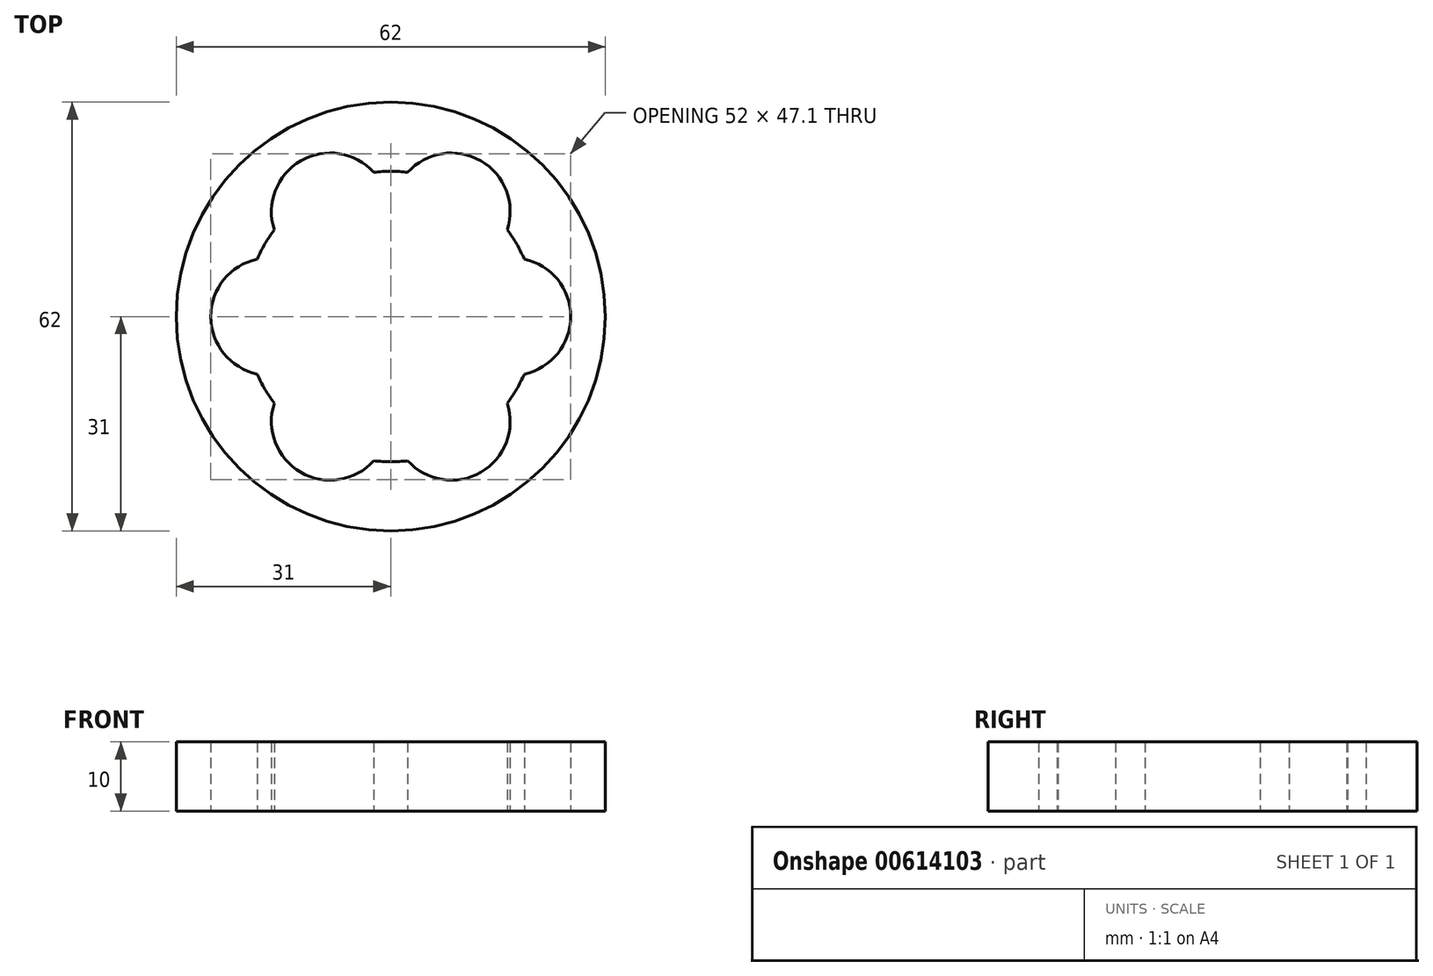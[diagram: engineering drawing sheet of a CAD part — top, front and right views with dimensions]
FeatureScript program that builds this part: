
annotation { "Feature Type Name" : "Feature", "Feature Type Description" : "" }
export const myFeature = defineFeature(function(context is Context, id is Id, definition is map)
    precondition{}
    {
        {
            var Q0;
            Q0=qCreatedBy(makeId("Top.planeOp"),FACE);
            var sketch = newSketch(context, id + "F0", { "sketchPlane" : qUnion([Q0])});
            skCircle(sketch, "E0", {"center": v(0, 0) * mm, "radius": 7 * mm});
            skCircle(sketch, "E1", {"center": v(17.5, 0) * mm, "radius": 8.5 * mm});
            skCircle(sketch, "E2.1.0", {"center": v(8.75, 15.16) * mm, "radius": 8.5 * mm});
            skCircle(sketch, "E2.2.0", {"center": v(-8.75, 15.16) * mm, "radius": 8.5 * mm});
            skCircle(sketch, "E2.3.0", {"center": v(-17.5, 0) * mm, "radius": 8.5 * mm});
            skCircle(sketch, "E2.4.0", {"center": v(-8.75, -15.16) * mm, "radius": 8.5 * mm});
            skCircle(sketch, "E2.5.0", {"center": v(8.75, -15.16) * mm, "radius": 8.5 * mm});
            skCircle(sketch, "E3", {"center": v(0, 0) * mm, "radius": 21 * mm});
            skCircle(sketch, "E4", {"center": v(0, 0) * mm, "radius": 31 * mm});
            skSolve(sketch);
        }
        {
            var Q0;
            Q0=makeQuery(id+"F0.imprint","IMPRINT",FACE,{"disambiguationData":[TD([[makeQuery(id+"F0.imprint","IMPRINT",EDGE,{"derivedFrom":sQuery(id+"F0.wireOp",EDGE,"VCIgbswB-IoET-C4wx-rXS6-aieKQBffOlC8")}),-1.0]])]});
            var Q1;
            Q1=makeQuery(id+"F0.imprint","IMPRINT",FACE,{"disambiguationData":[TD([[makeQuery(id+"F0.imprint","IMPRINT",EDGE,{"derivedFrom":sQuery(id+"F0.wireOp",EDGE,"E4")}),1.0]])]});
            extrude(context, id + "F1", {"entities" : qUnion([Q0, Q1]), "depth" : 10 * mm, "offsetDistance" : 25 * mm});
        }
    });
